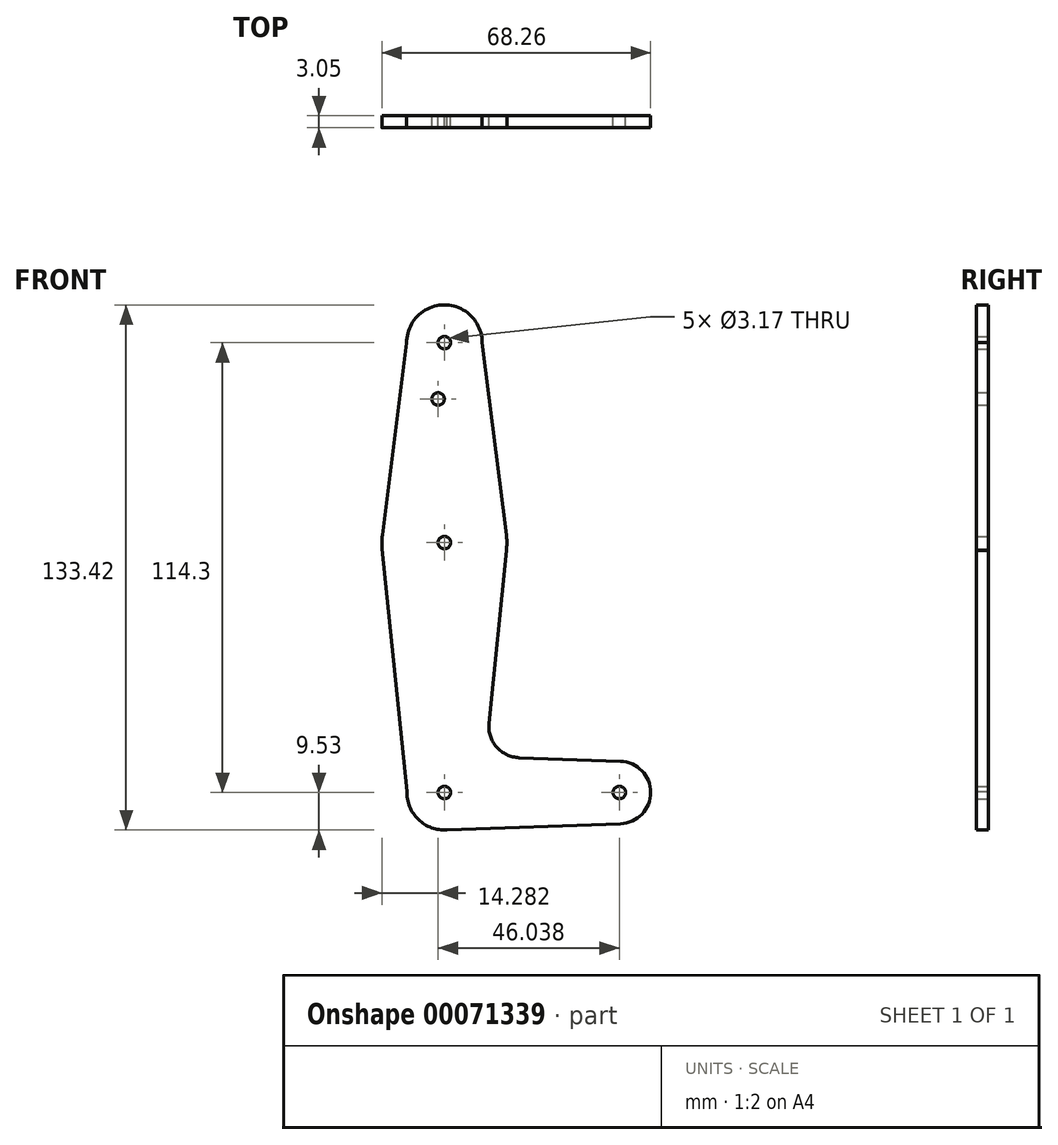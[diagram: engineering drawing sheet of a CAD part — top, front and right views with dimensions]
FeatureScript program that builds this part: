
annotation { "Feature Type Name" : "Feature", "Feature Type Description" : "" }
export const myFeature = defineFeature(function(context is Context, id is Id, definition is map)
    precondition{}
    {
        {
            var Q0;
            Q0=qCreatedBy(makeId("Front.planeOp"),FACE);
            var sketch = newSketch(context, id + "F0", { "sketchPlane" : qUnion([Q0])});
            skLineSegment(sketch, "E0", {"start": v(0, 50.8) * mm, "end": v(0, -63.5) * mm, "construction": true});
            skCircle(sketch, "E1", {"center": v(0, 0) * mm, "radius": 15.88 * mm});
            skCircle(sketch, "E2", {"center": v(0, 50.8) * mm, "radius": 9.59 * mm});
            skCircle(sketch, "E3", {"center": v(0, -63.5) * mm, "radius": 9.53 * mm});
            skLineSegment(sketch, "E4", {"start": v(0, -63.5) * mm, "end": v(44.45, -63.5) * mm, "construction": true});
            skCircle(sketch, "E5", {"center": v(44.45, -63.5) * mm, "radius": 7.94 * mm});
            skLineSegment(sketch, "E6", {"start": v(-9.59, 50.67) * mm, "end": v(-15.75, 2) * mm});
            skLineSegment(sketch, "E7", {"start": v(-9.52, -63.16) * mm, "end": v(-15.8, -1.6) * mm});
            skLineSegment(sketch, "E8", {"start": v(9.59, 50.8) * mm, "end": v(15.75, 1.99) * mm});
            skLineSegment(sketch, "E9", {"start": v(0, -73.03) * mm, "end": v(44.73, -71.43) * mm});
            skCircle(sketch, "E10", {"center": v(0, 50.8) * mm, "radius": 1.59 * mm});
            skCircle(sketch, "E11", {"center": v(0, 0) * mm, "radius": 1.59 * mm});
            skCircle(sketch, "E12", {"center": v(0, -63.5) * mm, "radius": 1.59 * mm});
            skCircle(sketch, "E13", {"center": v(44.45, -63.5) * mm, "radius": 1.59 * mm});
            skCircle(sketch, "E14", {"center": v(-1.59, 36.5) * mm, "radius": 1.59 * mm});
            skLineSegment(sketch, "E15", {"start": v(44.73, -55.57) * mm, "end": v(18.97, -54.65) * mm});
            skLineSegment(sketch, "E16", {"start": v(11.34, -45.91) * mm, "end": v(15.75, -1.99) * mm});
            skPoint(sketch, "E17.visualSharp", {"position": v(10.5, -54.35) * mm});
            skArc(sketch, "E17.filletArc", {"start": v(11.34, -45.91) * mm, "mid": v(13.26, -51.93) * mm, "end": v(18.97, -54.65) * mm});
            skSolve(sketch);
        }
        {
            var Q0;
            Q0 = qSketchRegion(id + "F0", true);
            extrude(context, id + "F1", {"entities" : qUnion([Q0]), "depth" : 3.05 * mm});
        }
    });
